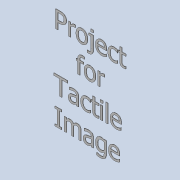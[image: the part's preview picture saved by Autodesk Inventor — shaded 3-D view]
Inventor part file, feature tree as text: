
AUTODESK INVENTOR PART (.ipt)
format: ipt  version: 2020 (Build 240168000, 168)  size: 625,664 bytes
history: native  units: mm
features: extrude x1, sketch x1
ambient origin geometry x8: Origin, YZ Plane, XZ Plane, XY Plane, X Axis, Y Axis, Z Axis, Center Point
bodies: Solid1 (feature_tree)
feature tree (2):
  extrude  "Extrusion1"  Depth=200.0mm
  sketch  "Sketch1"  dims[d0=300.0mm d1=200.0mm d2=0.6mm d3=0.0mm d4=50.0mm d5=50.0mm d6=20.0mm]
